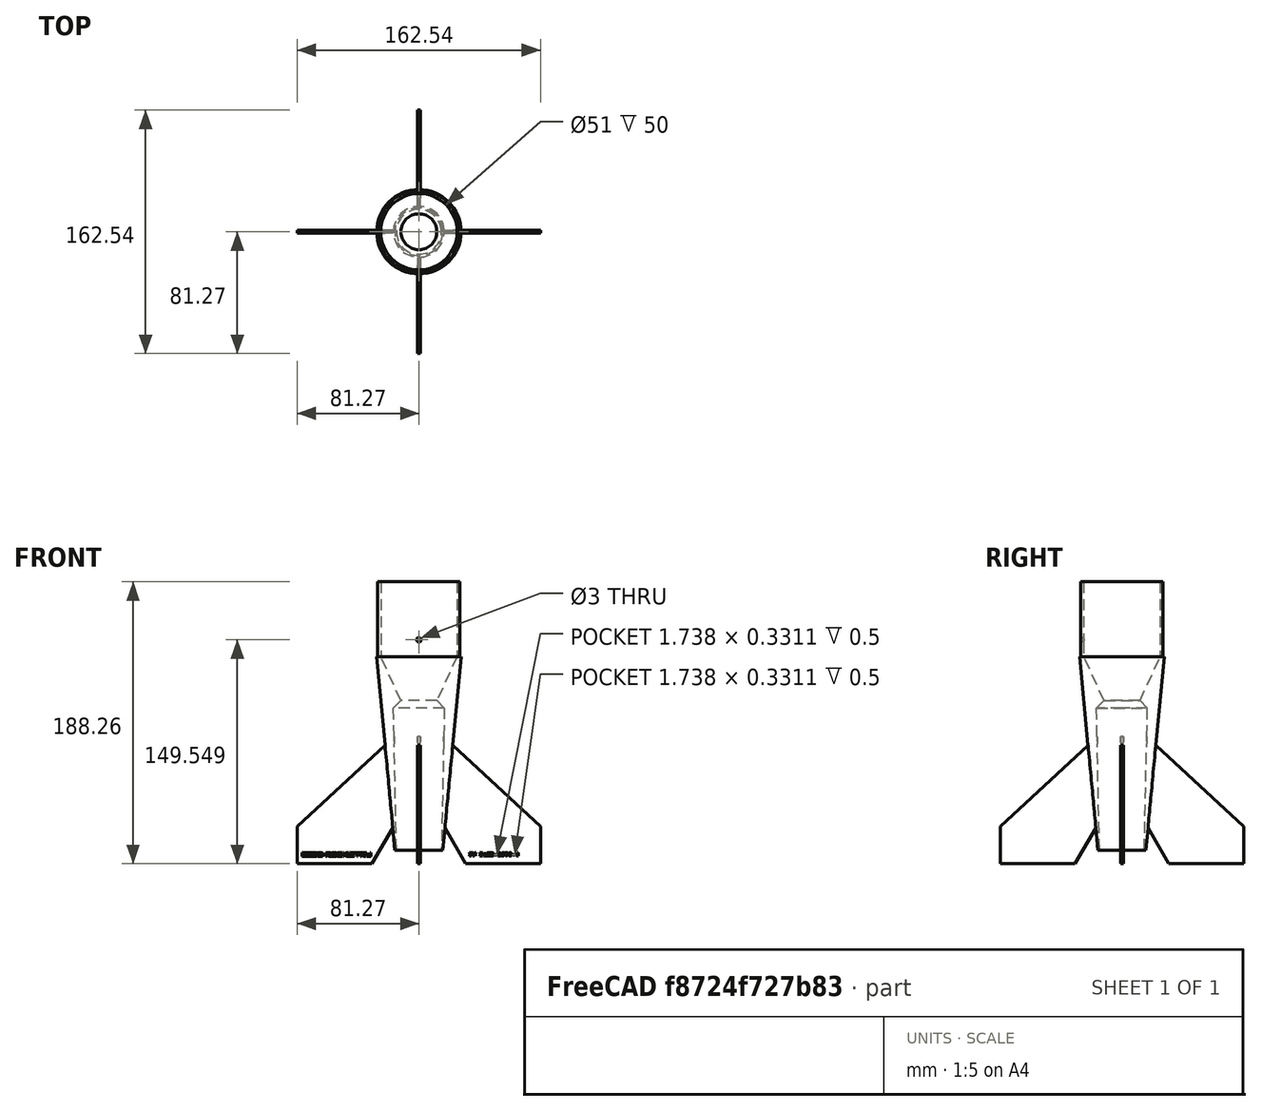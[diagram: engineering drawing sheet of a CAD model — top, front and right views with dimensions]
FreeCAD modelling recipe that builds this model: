
FCSTD DOCUMENT  (FreeCAD 0.20R29603 (Git))
Label: Ez3D-2970-4
License: All rights reserved
LicenseURL: http://en.wikipedia.org/wiki/All_rights_reserved
objects: Sketcher::SketchObject×3, Part::Part2DObjectPython×2, PartDesign::Pocket×2, PartDesign::Revolution×1, PartDesign::Pad×1, PartDesign::PolarPattern×1, PartDesign::Plane×1, PartDesign::Hole×1, PartDesign::Body×1, Mesh::Feature×1
note: 18 computed .brp shape members not serialized (recipe doc carries the construction recipe); baked Part::Feature solids carry a one-line shape summary decoded from their .brp

FEATURE [Sketcher::SketchObject] Sketch  label="Motor Mount001"
  FullyConstrained = false
  MapMode = 5
  Placement = pos=(0,0,0) rot=(1,0,0;1.5708rad)
  Support = -> [XZ_Plane]
  sketch-geometry (9):
    g0: LineSegment StartX=15 StartY=9 StartZ=0 EndX=16 EndY=9 EndZ=0
    g1: LineSegment StartX=12 StartY=109 StartZ=0 EndX=17 EndY=104 EndZ=0
    g2: LineSegment StartX=17 StartY=104 StartZ=0 EndX=15 EndY=9 EndZ=0
    g3: LineSegment StartX=16 StartY=9 StartZ=0 EndX=28.2 EndY=138.265 EndZ=0
    g4: LineSegment StartX=25.5 StartY=188.265 StartZ=0 EndX=25.5 EndY=138.265 EndZ=0
    g5: LineSegment StartX=25.5 StartY=138.265 StartZ=0 EndX=12 EndY=109 EndZ=0
    g6: LineSegment StartX=28.2 StartY=138.265 StartZ=0 EndX=27.5 EndY=138.265 EndZ=0
    g7: LineSegment StartX=27.5 StartY=138.265 StartZ=0 EndX=27.5 EndY=188.265 EndZ=0
    g8: LineSegment StartX=27.5 StartY=188.265 StartZ=0 EndX=25.5 EndY=188.265 EndZ=0
  constraints (26):
    c: Coincident(g1,g2)
    c: Coincident(g2,g0)
    c: DistanceX(g0,g0) = 1
    c: DistanceX(g-1,g0) = 15
    c: Angle(g1) = -0.785398
    c: Vertical(g4)
    c: Coincident(g4,g5)
    c: Coincident(g3,g6)
    c: Coincident(g6,g7)
    c: Vertical(g7)
    c: Coincident(g7,g8)
    c: Coincident(g8,g4)
    c: Horizontal(g8)
    c: Horizontal(g6)
    c: DistanceX(g-1,g7) = 27.5
    c: DistanceX(g8,g8) = 2
    c: Horizontal(g4,g6)
    c: DistanceY(g4,g4) = 50
    c: DistanceX(g6,g6) = 0.7
    c: Coincident(g5,g1)
    c: Coincident(g3,g0)
    c: DistanceX(g-1,g1) = 12
    c: DistanceX(g-1,g1) = 17
    c: Horizontal(g0)
    c: DistanceY(g-1,g0) = 9
    c: DistanceY(g-1,g1) = 104
FEATURE [PartDesign::Revolution] Revolution  label="Motor Mount"
  Angle = 360
  Axis = (0,-2e-16,1)
  Base = (0,0,0)
  Placement = pos=(0,0,0) rot=(1,0,0;1.5708rad)
  Profile = -> Sketch
  ReferenceAxis = -> Sketch [V_Axis]
  Reversed = true
FEATURE [Sketcher::SketchObject] Sketch001  label="Fins"
  FullyConstrained = false
  MapMode = 5
  Placement = pos=(0,0,0) rot=(1,0,0;1.5708rad)
  Support = -> [XZ_Plane]
  sketch-geometry (5):
    g0: LineSegment StartX=31.2658 StartY=0 StartZ=0 EndX=81.2658 EndY=-1e-16 EndZ=0
    g1: LineSegment StartX=81.2658 StartY=-1e-16 StartZ=0 EndX=81.2658 EndY=25 EndZ=0
    g2: LineSegment StartX=81.2658 StartY=25 StartZ=0 EndX=16.5 EndY=85 EndZ=0
    g3: LineSegment StartX=16.5 StartY=85 StartZ=0 EndX=16.5 EndY=25.5751 EndZ=0
    g4: LineSegment StartX=16.5 StartY=25.5751 StartZ=0 EndX=31.2658 EndY=0 EndZ=0
  constraints (13):
    c: Coincident(g0,g1)
    c: Coincident(g1,g2)
    c: Vertical(g1)
    c: Coincident(g2,g3)
    c: Vertical(g3)
    c: Coincident(g3,g4)
    c: Coincident(g0,g4)
    c: DistanceX(g-1,g2) = 16.5
    c: Angle(g4) = -1.0472
    c: DistanceX(g0,g0) = 50
    c: DistanceY(g1,g1) = 25
    c: DistanceY(g1,g2) = 60
    c: Tangent(g0,g-1)
FEATURE [PartDesign::Pad] Pad  label="Fins Pad"
  BaseFeature = -> Revolution
  Direction = (0,-1,-2e-16)
  Length = 2
  Length2 = 100
  Midplane = true
  Placement = pos=(0,0,0) rot=(1,0,0;1.5708rad)
  Profile = -> Sketch001
  Type = 0
FEATURE [PartDesign::PolarPattern] PolarPattern
  Angle = 360
  Axis = -> Z_Axis
  BaseFeature = -> Pad
  Occurrences = 4
  Originals = -> [Pad]
  Placement = pos=(0,0,0) rot=(1,0,0;1.5708rad)
FEATURE [PartDesign::Plane] DatumPlane
  Length = 199.767
  MapMode = 5
  Placement = pos=(0,1,-1.4e-15) rot=(-1,0,0;1.5708rad)
  ResizeMode = 0
  Support = -> [PolarPattern]
  Width = 250.501
FEATURE [Sketcher::SketchObject] Sketch002
  FullyConstrained = false
  MapMode = 5
  Placement = pos=(0,1,-1.4e-15) rot=(-1,0,0;1.5708rad)
  Support = -> [DatumPlane]
  sketch-geometry (1):
    g0: Circle CenterX=0 CenterY=-149.549 CenterZ=0 NormalX=0 NormalY=0 NormalZ=1 AngleXU=0 Radius=6.87884
  constraints (1):
    c: PointOnObject(g0,g-2)
FEATURE [PartDesign::Hole] Hole
  BaseFeature = -> PolarPattern
  CustomThreadClearance = 0
  Depth = 32
  DepthType = 0
  Diameter = 3
  DrillForDepth = false
  DrillPoint = 1
  DrillPointAngle = 118
  HoleCutCountersinkAngle = 90
  HoleCutCustomValues = false
  HoleCutDepth = 0
  HoleCutDiameter = 6.1
  HoleCutType = 0
  ModelThread = false
  Placement = pos=(0,0,0) rot=(1,0,0;1.5708rad)
  Profile = -> Sketch002
  Tapered = false
  TaperedAngle = 90
  ThreadClass = 0
  ThreadDepth = 32
  ThreadDepthType = 0
  ThreadDirection = 0
  ThreadFit = 0
  ThreadSize = 0
  ThreadType = 0
  Threaded = false
  UseCustomThreadClearance = false
FEATURE [Part::Part2DObjectPython] ShapeString  # Draft 2D object (typed FeaturePython)
  FontFile = <path>
  MakeFace = true
  Placement = pos=(-78.35,-1,4.748) rot=(1,0,0;1.5708rad)
  Size = 1.5
  String = Ez3D Rocketry
  Tracking = 0
FEATURE [Part::Part2DObjectPython] ShapeString001  # Draft 2D object (typed FeaturePython)
  FontFile = <path>
  MakeFace = true
  Placement = pos=(33.307,-1,5.067) rot=(1,0,0;1.5708rad)
  Size = 3
  String = PN Ez3D-2970-4
  Tracking = 0
FEATURE [PartDesign::Pocket] Pocket
  BaseFeature = -> Hole
  Direction = (0,1,0)
  Length = 0.5
  Length2 = 5
  Placement = pos=(0,0,0) rot=(1,0,0;1.5708rad)
  Profile = -> ShapeString
  ReferenceAxis = -> ShapeString [N_Axis]
  Type = 0
FEATURE [PartDesign::Pocket] Pocket001
  BaseFeature = -> Pocket
  Direction = (2e-16,1,-7e-16)
  Length = 0.5
  Length2 = 5
  Placement = pos=(0,0,0) rot=(1,0,0;1.5708rad)
  Profile = -> ShapeString001
  ReferenceAxis = -> ShapeString001 [N_Axis]
  Type = 0
FEATURE [PartDesign::Body] Body
  Group = -> [Sketch,Revolution,Sketch001,Pad,PolarPattern,DatumPlane,Sketch002,Hole,ShapeString,ShapeString001,Pocket,Pocket001]
  Origin = -> Origin
  Tip = -> Pocket001
FEATURE [Mesh::Feature] For_29mm_M36x4___10mm_high___14_6mm_Radius  label="For 29mm M36x4 - 10mm high - 14.6mm Radius"
note: 2 file-system paths scrubbed to <path> (originals preserved in the JSON sidecar)
